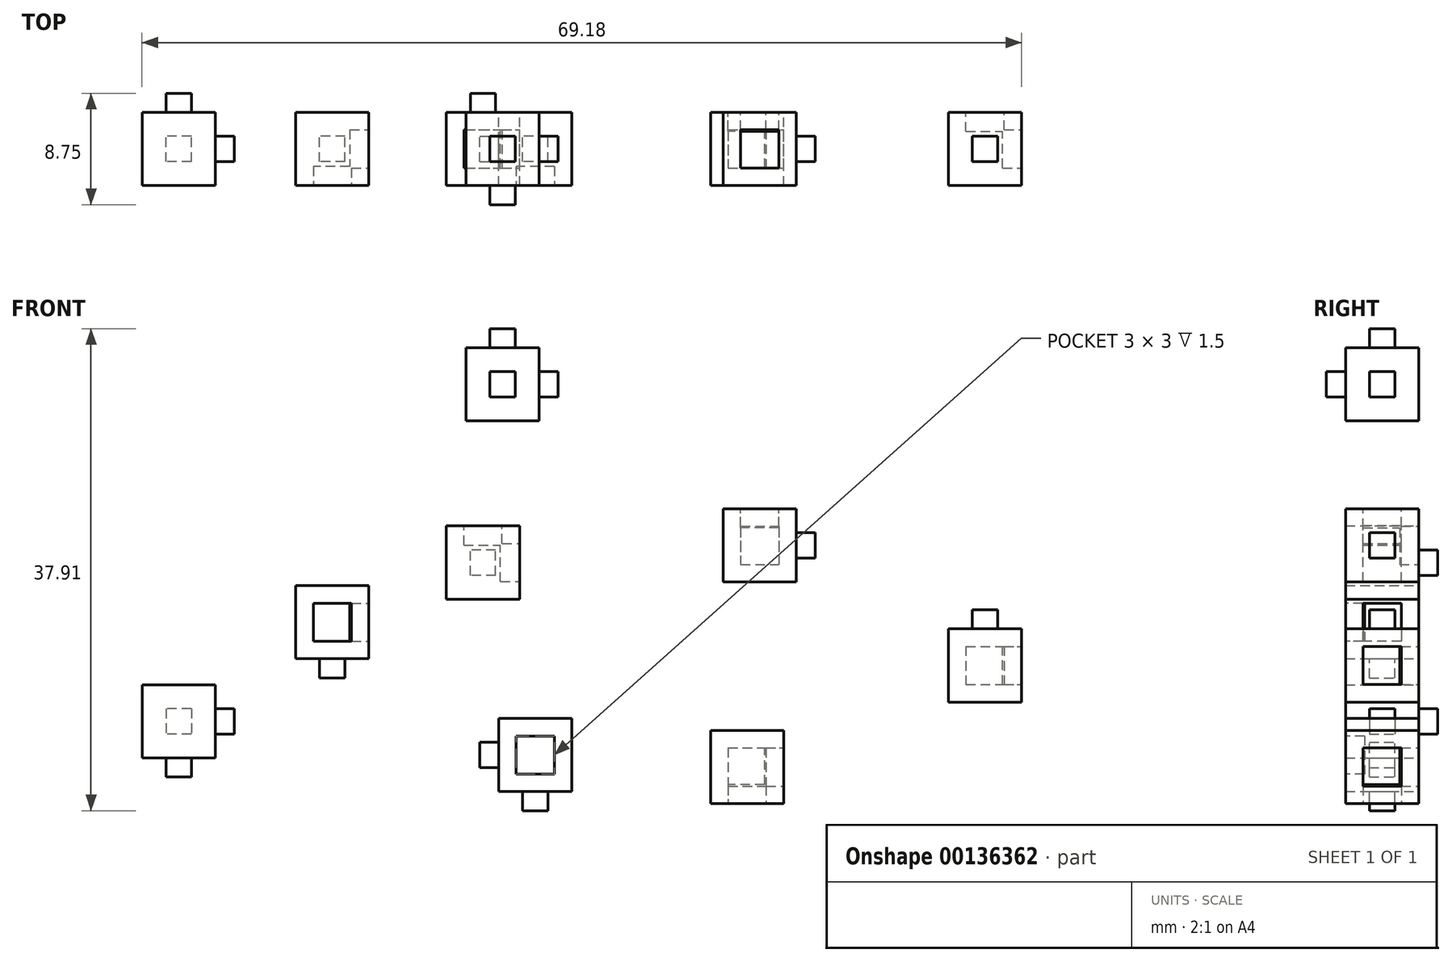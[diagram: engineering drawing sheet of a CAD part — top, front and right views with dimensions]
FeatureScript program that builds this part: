
annotation { "Feature Type Name" : "Feature", "Feature Type Description" : "" }
export const myFeature = defineFeature(function(context is Context, id is Id, definition is map)
    precondition{}
    {
        {
            var Q0;
            Q0=qCreatedBy(makeId("Front.planeOp"),FACE);
            var sketch = newSketch(context, id + "F0", { "sketchPlane" : qUnion([Q0])});
            skLineSegment(sketch, "E0.bottom", {"start": v(-17.05, 10.62) * mm, "end": v(-11.3, 10.62) * mm});
            skLineSegment(sketch, "E0.top", {"start": v(-17.05, 4.87) * mm, "end": v(-11.3, 4.87) * mm});
            skLineSegment(sketch, "E0.left", {"start": v(-17.05, 10.62) * mm, "end": v(-17.05, 4.87) * mm});
            skLineSegment(sketch, "E0.right", {"start": v(-11.3, 10.62) * mm, "end": v(-11.3, 4.87) * mm});
            skLineSegment(sketch, "E1.bottom", {"start": v(4.72, 11.97) * mm, "end": v(10.47, 11.97) * mm});
            skLineSegment(sketch, "E1.top", {"start": v(4.72, 6.22) * mm, "end": v(10.47, 6.22) * mm});
            skLineSegment(sketch, "E1.left", {"start": v(4.72, 11.97) * mm, "end": v(4.72, 6.22) * mm});
            skLineSegment(sketch, "E1.right", {"start": v(10.47, 11.97) * mm, "end": v(10.47, 6.22) * mm});
            skLineSegment(sketch, "E2.bottom", {"start": v(3.72, -5.46) * mm, "end": v(9.47, -5.46) * mm});
            skLineSegment(sketch, "E2.top", {"start": v(3.72, -11.2) * mm, "end": v(9.47, -11.2) * mm});
            skLineSegment(sketch, "E2.left", {"start": v(3.72, -5.46) * mm, "end": v(3.72, -11.2) * mm});
            skLineSegment(sketch, "E2.right", {"start": v(9.47, -5.46) * mm, "end": v(9.47, -11.2) * mm});
            skLineSegment(sketch, "E3.bottom", {"start": v(-12.94, -4.52) * mm, "end": v(-7.19, -4.52) * mm});
            skLineSegment(sketch, "E3.top", {"start": v(-12.94, -10.27) * mm, "end": v(-7.19, -10.27) * mm});
            skLineSegment(sketch, "E3.left", {"start": v(-12.94, -4.52) * mm, "end": v(-12.94, -10.27) * mm});
            skLineSegment(sketch, "E3.right", {"start": v(-7.19, -4.52) * mm, "end": v(-7.19, -10.27) * mm});
            skLineSegment(sketch, "E4.bottom", {"start": v(22.44, 2.52) * mm, "end": v(28.2, 2.52) * mm});
            skLineSegment(sketch, "E4.top", {"start": v(22.44, -3.23) * mm, "end": v(28.2, -3.23) * mm});
            skLineSegment(sketch, "E4.left", {"start": v(22.44, 2.52) * mm, "end": v(22.44, -3.23) * mm});
            skLineSegment(sketch, "E4.right", {"start": v(28.2, 2.52) * mm, "end": v(28.2, -3.23) * mm});
            skLineSegment(sketch, "E5.bottom", {"start": v(-28.9, 5.92) * mm, "end": v(-23.15, 5.92) * mm});
            skLineSegment(sketch, "E5.top", {"start": v(-28.9, 0.17) * mm, "end": v(-23.15, 0.17) * mm});
            skLineSegment(sketch, "E5.left", {"start": v(-28.9, 5.92) * mm, "end": v(-28.9, 0.17) * mm});
            skLineSegment(sketch, "E5.right", {"start": v(-23.15, 5.92) * mm, "end": v(-23.15, 0.17) * mm});
            skLineSegment(sketch, "E6.bottom", {"start": v(-35.24, -1.88) * mm, "end": v(-40.99, -1.88) * mm});
            skLineSegment(sketch, "E6.top", {"start": v(-35.24, -7.63) * mm, "end": v(-40.99, -7.63) * mm});
            skLineSegment(sketch, "E6.left", {"start": v(-35.24, -1.88) * mm, "end": v(-35.24, -7.63) * mm});
            skLineSegment(sketch, "E6.right", {"start": v(-40.99, -1.88) * mm, "end": v(-40.99, -7.63) * mm});
            skLineSegment(sketch, "E7.bottom", {"start": v(-15.52, 24.64) * mm, "end": v(-9.77, 24.64) * mm});
            skLineSegment(sketch, "E7.top", {"start": v(-15.52, 18.9) * mm, "end": v(-9.77, 18.9) * mm});
            skLineSegment(sketch, "E7.left", {"start": v(-15.52, 24.64) * mm, "end": v(-15.52, 18.9) * mm});
            skLineSegment(sketch, "E7.right", {"start": v(-9.77, 24.64) * mm, "end": v(-9.77, 18.9) * mm});
            skSolve(sketch);
        }
        {
            var Q0;
            Q0=makeQuery(id+"F0.imprint","IMPRINT",FACE,{"disambiguationData":[TD([[makeQuery(id+"F0.imprint","IMPRINT",EDGE,{"derivedFrom":sQuery(id+"F0.wireOp",EDGE,"E7.bottom")}),-1.0]])]});
            var Q1;
            Q1=makeQuery(id+"F0.imprint","IMPRINT",FACE,{"disambiguationData":[TD([[makeQuery(id+"F0.imprint","IMPRINT",EDGE,{"derivedFrom":sQuery(id+"F0.wireOp",EDGE,"E0.bottom")}),-1.0]])]});
            var Q2;
            Q2=makeQuery(id+"F0.imprint","IMPRINT",FACE,{"disambiguationData":[TD([[makeQuery(id+"F0.imprint","IMPRINT",EDGE,{"derivedFrom":sQuery(id+"F0.wireOp",EDGE,"E5.bottom")}),-1.0]])]});
            var Q3;
            Q3=makeQuery(id+"F0.imprint","IMPRINT",FACE,{"disambiguationData":[TD([[makeQuery(id+"F0.imprint","IMPRINT",EDGE,{"derivedFrom":sQuery(id+"F0.wireOp",EDGE,"E6.bottom")}),1.0]])]});
            var Q4;
            Q4=makeQuery(id+"F0.imprint","IMPRINT",FACE,{"disambiguationData":[TD([[makeQuery(id+"F0.imprint","IMPRINT",EDGE,{"derivedFrom":sQuery(id+"F0.wireOp",EDGE,"E3.bottom")}),-1.0]])]});
            var Q5;
            Q5=makeQuery(id+"F0.imprint","IMPRINT",FACE,{"disambiguationData":[TD([[makeQuery(id+"F0.imprint","IMPRINT",EDGE,{"derivedFrom":sQuery(id+"F0.wireOp",EDGE,"E2.bottom")}),-1.0]])]});
            var Q6;
            Q6=makeQuery(id+"F0.imprint","IMPRINT",FACE,{"disambiguationData":[TD([[makeQuery(id+"F0.imprint","IMPRINT",EDGE,{"derivedFrom":sQuery(id+"F0.wireOp",EDGE,"E1.bottom")}),-1.0]])]});
            var Q7;
            Q7=makeQuery(id+"F0.imprint","IMPRINT",FACE,{"disambiguationData":[TD([[makeQuery(id+"F0.imprint","IMPRINT",EDGE,{"derivedFrom":sQuery(id+"F0.wireOp",EDGE,"E4.bottom")}),-1.0]])]});
            extrude(context, id + "F1", {"entities" : qUnion([Q0, Q1, Q2, Q3, Q4, Q5, Q6, Q7]), "depth" : 5.75 * mm});
        }
        {
            var Q0;
            Q0=makeQuery(id+"F1.opExtrude","CAP_FACE",FACE,{"disambiguationData":[OSD([sQuery(id+"F0.wireOp",EDGE,"E5.bottom"),sQuery(id+"F0.wireOp",EDGE,"E5.top"),sQuery(id+"F0.wireOp",EDGE,"E5.left"),sQuery(id+"F0.wireOp",EDGE,"E5.right")])],"isStart":false});
            var sketch = newSketch(context, id + "F2", { "sketchPlane" : qUnion([Q0])});
            skLineSegment(sketch, "E8.bottom", {"start": v(-24.52, 4.55) * mm, "end": v(-27.52, 4.55) * mm});
            skLineSegment(sketch, "E8.top", {"start": v(-24.52, 1.55) * mm, "end": v(-27.52, 1.55) * mm});
            skLineSegment(sketch, "E8.left", {"start": v(-24.52, 4.55) * mm, "end": v(-24.52, 1.55) * mm});
            skLineSegment(sketch, "E8.right", {"start": v(-27.52, 4.55) * mm, "end": v(-27.52, 1.55) * mm});
            skPoint(sketch, "E8.middle", {"position": v(-26.02, 3.05) * mm});
            skPoint(sketch, "E8.middle.positionSnap0", {"position": v(-28.9, 3.05) * mm});
            skPoint(sketch, "E8.middle.positionSnap1", {"position": v(-26.02, 5.92) * mm});
            skPoint(sketch, "E8.centerSnap0", {"position": v(-28.9, 3.05) * mm});
            skPoint(sketch, "E8.centerSnap1", {"position": v(-26.02, 5.92) * mm});
            skSolve(sketch);
        }
        {
            var Q0;
            Q0=makeQuery(id+"F1.opExtrude","SWEPT_FACE",FACE,{"disambiguationData":[OSD([sQuery(id+"F0.wireOp",EDGE,"E5.top")])]});
            var sketch = newSketch(context, id + "F3", { "sketchPlane" : qUnion([Q0])});
            skLineSegment(sketch, "E9.bottom", {"start": v(-25.02, 3.88) * mm, "end": v(-27.02, 3.88) * mm});
            skLineSegment(sketch, "E9.top", {"start": v(-25.02, 1.87) * mm, "end": v(-27.02, 1.87) * mm});
            skLineSegment(sketch, "E9.left", {"start": v(-25.02, 3.88) * mm, "end": v(-25.02, 1.88) * mm});
            skLineSegment(sketch, "E9.right", {"start": v(-27.02, 3.88) * mm, "end": v(-27.02, 1.88) * mm});
            skPoint(sketch, "E9.middle", {"position": v(-26.02, 2.88) * mm});
            skPoint(sketch, "E9.middle.positionSnap0", {"position": v(-28.9, 2.88) * mm});
            skPoint(sketch, "E9.middle.positionSnap1", {"position": v(-26.02, 5.75) * mm});
            skPoint(sketch, "E9.centerSnap0", {"position": v(-28.9, 2.88) * mm});
            skPoint(sketch, "E9.centerSnap1", {"position": v(-26.02, 5.75) * mm});
            skSolve(sketch);
        }
        {
            var Q0;
            Q0=makeQuery(id+"F2.imprint","IMPRINT",FACE,{"disambiguationData":[TD([[makeQuery(id+"F2.imprint","IMPRINT",EDGE,{"derivedFrom":sQuery(id+"F2.wireOp",EDGE,"E8.bottom")}),1.0]])]});
            extrude(context, id + "F4", {"entities" : qUnion([Q0]), "operationType" : NewBodyOperationType.REMOVE, "oppositeDirection" : true, "depth" : 1.5 * mm});
        }
        {
            var Q0;
            Q0=makeQuery(id+"F3.imprint","IMPRINT",FACE,{"disambiguationData":[TD([[makeQuery(id+"F3.imprint","IMPRINT",EDGE,{"derivedFrom":sQuery(id+"F3.wireOp",EDGE,"E9.bottom")}),1.0]])]});
            extrude(context, id + "F5", {"entities" : qUnion([Q0]), "operationType" : NewBodyOperationType.ADD, "depth" : 1.5 * mm});
        }
        {
            var Q0;
            Q0=makeQuery(id+"F1.opExtrude","SWEPT_FACE",FACE,{"disambiguationData":[OSD([sQuery(id+"F0.wireOp",EDGE,"E5.right")])]});
            var sketch = newSketch(context, id + "F6", { "sketchPlane" : qUnion([Q0])});
            skLineSegment(sketch, "E10.bottom", {"start": v(-1.38, 4.55) * mm, "end": v(-4.38, 4.55) * mm});
            skLineSegment(sketch, "E10.top", {"start": v(-1.38, 1.55) * mm, "end": v(-4.38, 1.55) * mm});
            skLineSegment(sketch, "E10.left", {"start": v(-1.38, 4.55) * mm, "end": v(-1.38, 1.55) * mm});
            skLineSegment(sketch, "E10.right", {"start": v(-4.38, 4.55) * mm, "end": v(-4.38, 1.55) * mm});
            skPoint(sketch, "E10.middle", {"position": v(-2.88, 3.05) * mm});
            skPoint(sketch, "E10.middle.positionSnap0", {"position": v(-2.88, 0.17) * mm});
            skPoint(sketch, "E10.middle.positionSnap1", {"position": v(-5.75, 3.05) * mm});
            skPoint(sketch, "E10.centerSnap0", {"position": v(-2.88, 0.17) * mm});
            skPoint(sketch, "E10.centerSnap1", {"position": v(-5.75, 3.05) * mm});
            skSolve(sketch);
        }
        {
            var Q0;
            Q0 = qSketchRegion(id + "F6", true);
            extrude(context, id + "F7", {"entities" : qUnion([Q0]), "operationType" : NewBodyOperationType.REMOVE, "oppositeDirection" : true, "depth" : 1.5 * mm});
        }
        {
            var Q0;
            Q0=makeQuery(id+"F1.opExtrude","CAP_FACE",FACE,{"disambiguationData":[OSD([sQuery(id+"F0.wireOp",EDGE,"E6.bottom"),sQuery(id+"F0.wireOp",EDGE,"E6.top"),sQuery(id+"F0.wireOp",EDGE,"E6.left"),sQuery(id+"F0.wireOp",EDGE,"E6.right")])],"isStart":true});
            var sketch = newSketch(context, id + "F8", { "sketchPlane" : qUnion([Q0])});
            skLineSegment(sketch, "E11.bottom", {"start": v(37.11, -3.75) * mm, "end": v(39.11, -3.75) * mm});
            skLineSegment(sketch, "E11.top", {"start": v(37.11, -5.75) * mm, "end": v(39.11, -5.75) * mm});
            skLineSegment(sketch, "E11.left", {"start": v(37.11, -3.75) * mm, "end": v(37.11, -5.75) * mm});
            skLineSegment(sketch, "E11.right", {"start": v(39.11, -3.75) * mm, "end": v(39.11, -5.75) * mm});
            skPoint(sketch, "E11.middle", {"position": v(38.11, -4.75) * mm});
            skPoint(sketch, "E11.middle.positionSnap0", {"position": v(40.99, -4.75) * mm});
            skPoint(sketch, "E11.middle.positionSnap1", {"position": v(38.11, -7.63) * mm});
            skPoint(sketch, "E11.centerSnap0", {"position": v(40.99, -4.75) * mm});
            skPoint(sketch, "E11.centerSnap1", {"position": v(38.11, -7.63) * mm});
            skSolve(sketch);
        }
        {
            var Q0;
            Q0=makeQuery(id+"F8.imprint","IMPRINT",FACE,{"disambiguationData":[TD([[makeQuery(id+"F8.imprint","IMPRINT",EDGE,{"derivedFrom":sQuery(id+"F8.wireOp",EDGE,"E11.bottom")}),-1.0]])]});
            extrude(context, id + "F9", {"entities" : qUnion([Q0]), "operationType" : NewBodyOperationType.ADD, "depth" : 1.5 * mm});
        }
        {
            var Q0;
            Q0=makeQuery(id+"F1.opExtrude","SWEPT_FACE",FACE,{"disambiguationData":[OSD([sQuery(id+"F0.wireOp",EDGE,"E6.left")])]});
            var sketch = newSketch(context, id + "F10", { "sketchPlane" : qUnion([Q0])});
            skLineSegment(sketch, "E12.bottom", {"start": v(-3.88, -3.75) * mm, "end": v(-1.88, -3.75) * mm});
            skLineSegment(sketch, "E12.top", {"start": v(-3.87, -5.75) * mm, "end": v(-1.88, -5.75) * mm});
            skLineSegment(sketch, "E12.left", {"start": v(-3.88, -3.75) * mm, "end": v(-3.87, -5.75) * mm});
            skLineSegment(sketch, "E12.right", {"start": v(-1.88, -3.75) * mm, "end": v(-1.88, -5.75) * mm});
            skPoint(sketch, "E12.middle", {"position": v(-2.88, -4.75) * mm});
            skPoint(sketch, "E12.middle.positionSnap0", {"position": v(-5.75, -4.75) * mm});
            skPoint(sketch, "E12.middle.positionSnap1", {"position": v(-2.88, -7.63) * mm});
            skPoint(sketch, "E12.centerSnap0", {"position": v(-5.75, -4.75) * mm});
            skPoint(sketch, "E12.centerSnap1", {"position": v(-2.88, -7.63) * mm});
            skSolve(sketch);
        }
        {
            var Q0;
            Q0=makeQuery(id+"F10.imprint","IMPRINT",FACE,{"disambiguationData":[TD([[makeQuery(id+"F10.imprint","IMPRINT",EDGE,{"derivedFrom":sQuery(id+"F10.wireOp",EDGE,"E12.bottom")}),-1.0]])]});
            extrude(context, id + "F11", {"entities" : qUnion([Q0]), "operationType" : NewBodyOperationType.ADD, "depth" : 1.5 * mm});
        }
        {
            var Q0;
            Q0=makeQuery(id+"F1.opExtrude","SWEPT_FACE",FACE,{"disambiguationData":[OSD([sQuery(id+"F0.wireOp",EDGE,"E6.top")])]});
            var sketch = newSketch(context, id + "F12", { "sketchPlane" : qUnion([Q0])});
            skLineSegment(sketch, "E13.bottom", {"start": v(-37.11, 3.87) * mm, "end": v(-39.11, 3.87) * mm});
            skLineSegment(sketch, "E13.top", {"start": v(-37.11, 1.87) * mm, "end": v(-39.11, 1.87) * mm});
            skLineSegment(sketch, "E13.left", {"start": v(-37.11, 3.87) * mm, "end": v(-37.11, 1.87) * mm});
            skLineSegment(sketch, "E13.right", {"start": v(-39.11, 3.87) * mm, "end": v(-39.11, 1.87) * mm});
            skPoint(sketch, "E13.middle", {"position": v(-38.11, 2.88) * mm});
            skPoint(sketch, "E13.middle.positionSnap0", {"position": v(-40.99, 2.88) * mm});
            skPoint(sketch, "E13.middle.positionSnap1", {"position": v(-38.11, 5.75) * mm});
            skPoint(sketch, "E13.centerSnap0", {"position": v(-40.99, 2.88) * mm});
            skPoint(sketch, "E13.centerSnap1", {"position": v(-38.11, 5.75) * mm});
            skSolve(sketch);
        }
        {
            var Q0;
            Q0 = qSketchRegion(id + "F12", true);
            extrude(context, id + "F13", {"entities" : qUnion([Q0]), "operationType" : NewBodyOperationType.ADD, "depth" : 1.5 * mm});
        }
        {
            var Q0;
            Q0=makeQuery(id+"F1.opExtrude","CAP_FACE",FACE,{"disambiguationData":[OSD([sQuery(id+"F0.wireOp",EDGE,"E3.bottom"),sQuery(id+"F0.wireOp",EDGE,"E3.top"),sQuery(id+"F0.wireOp",EDGE,"E3.left"),sQuery(id+"F0.wireOp",EDGE,"E3.right")])],"isStart":false});
            var sketch = newSketch(context, id + "F14", { "sketchPlane" : qUnion([Q0])});
            skLineSegment(sketch, "E14.bottom", {"start": v(-8.56, -5.9) * mm, "end": v(-11.56, -5.9) * mm});
            skLineSegment(sketch, "E14.top", {"start": v(-8.56, -8.9) * mm, "end": v(-11.56, -8.9) * mm});
            skLineSegment(sketch, "E14.left", {"start": v(-8.56, -5.9) * mm, "end": v(-8.56, -8.9) * mm});
            skLineSegment(sketch, "E14.right", {"start": v(-11.56, -5.9) * mm, "end": v(-11.56, -8.9) * mm});
            skPoint(sketch, "E14.middle", {"position": v(-10.06, -7.4) * mm});
            skPoint(sketch, "E14.middle.positionSnap0", {"position": v(-12.94, -7.4) * mm});
            skPoint(sketch, "E14.middle.positionSnap1", {"position": v(-10.06, -4.52) * mm});
            skPoint(sketch, "E14.centerSnap0", {"position": v(-12.94, -7.4) * mm});
            skPoint(sketch, "E14.centerSnap1", {"position": v(-10.06, -4.52) * mm});
            skSolve(sketch);
        }
        {
            var Q0;
            Q0 = qSketchRegion(id + "F14", true);
            extrude(context, id + "F15", {"entities" : qUnion([Q0]), "operationType" : NewBodyOperationType.REMOVE, "oppositeDirection" : true, "depth" : 1.5 * mm});
        }
        {
            var Q0;
            Q0=makeQuery(id+"F1.opExtrude","SWEPT_FACE",FACE,{"disambiguationData":[OSD([sQuery(id+"F0.wireOp",EDGE,"E3.top")])]});
            var sketch = newSketch(context, id + "F16", { "sketchPlane" : qUnion([Q0])});
            skLineSegment(sketch, "E15.bottom", {"start": v(-9.06, 3.87) * mm, "end": v(-11.06, 3.87) * mm});
            skLineSegment(sketch, "E15.top", {"start": v(-9.06, 1.87) * mm, "end": v(-11.06, 1.88) * mm});
            skLineSegment(sketch, "E15.left", {"start": v(-9.06, 3.87) * mm, "end": v(-9.06, 1.87) * mm});
            skLineSegment(sketch, "E15.right", {"start": v(-11.06, 3.87) * mm, "end": v(-11.06, 1.88) * mm});
            skPoint(sketch, "E15.middle", {"position": v(-10.06, 2.88) * mm});
            skPoint(sketch, "E15.middle.positionSnap0", {"position": v(-12.94, 2.88) * mm});
            skPoint(sketch, "E15.middle.positionSnap1", {"position": v(-10.06, 5.75) * mm});
            skPoint(sketch, "E15.centerSnap0", {"position": v(-12.94, 2.88) * mm});
            skPoint(sketch, "E15.centerSnap1", {"position": v(-10.06, 5.75) * mm});
            skSolve(sketch);
        }
        {
            var Q0;
            Q0=makeQuery(id+"F16.imprint","IMPRINT",FACE,{"disambiguationData":[TD([[makeQuery(id+"F16.imprint","IMPRINT",EDGE,{"derivedFrom":sQuery(id+"F16.wireOp",EDGE,"E15.bottom")}),1.0]])]});
            extrude(context, id + "F17", {"entities" : qUnion([Q0]), "operationType" : NewBodyOperationType.ADD, "depth" : 1.5 * mm});
        }
        {
            var Q0;
            Q0=makeQuery(id+"F1.opExtrude","SWEPT_FACE",FACE,{"disambiguationData":[OSD([sQuery(id+"F0.wireOp",EDGE,"E3.left")])]});
            var sketch = newSketch(context, id + "F18", { "sketchPlane" : qUnion([Q0])});
            skLineSegment(sketch, "E16.bottom", {"start": v(3.88, -8.4) * mm, "end": v(1.88, -8.4) * mm});
            skLineSegment(sketch, "E16.top", {"start": v(3.88, -6.4) * mm, "end": v(1.88, -6.4) * mm});
            skLineSegment(sketch, "E16.left", {"start": v(3.88, -8.4) * mm, "end": v(3.88, -6.4) * mm});
            skLineSegment(sketch, "E16.right", {"start": v(1.88, -8.4) * mm, "end": v(1.88, -6.4) * mm});
            skPoint(sketch, "E16.middle", {"position": v(2.88, -7.4) * mm});
            skPoint(sketch, "E16.middle.positionSnap0", {"position": v(2.88, -4.52) * mm});
            skPoint(sketch, "E16.middle.positionSnap1", {"position": v(5.75, -7.4) * mm});
            skPoint(sketch, "E16.centerSnap0", {"position": v(2.88, -4.52) * mm});
            skPoint(sketch, "E16.centerSnap1", {"position": v(5.75, -7.4) * mm});
            skSolve(sketch);
        }
        {
            var Q0;
            Q0 = qSketchRegion(id + "F18", true);
            extrude(context, id + "F19", {"entities" : qUnion([Q0]), "operationType" : NewBodyOperationType.ADD, "depth" : 1.5 * mm});
        }
        {
            var Q0;
            Q0=makeQuery(id+"F1.opExtrude","SWEPT_FACE",FACE,{"disambiguationData":[OSD([sQuery(id+"F0.wireOp",EDGE,"E4.right")])]});
            var sketch = newSketch(context, id + "F20", { "sketchPlane" : qUnion([Q0])});
            skLineSegment(sketch, "E17.bottom", {"start": v(-4.38, 1.15) * mm, "end": v(-1.37, 1.15) * mm});
            skLineSegment(sketch, "E17.top", {"start": v(-4.38, -1.85) * mm, "end": v(-1.38, -1.85) * mm});
            skLineSegment(sketch, "E17.left", {"start": v(-4.38, 1.15) * mm, "end": v(-4.38, -1.85) * mm});
            skLineSegment(sketch, "E17.right", {"start": v(-1.37, 1.15) * mm, "end": v(-1.38, -1.85) * mm});
            skPoint(sketch, "E17.middle", {"position": v(-2.88, -0.35) * mm});
            skPoint(sketch, "E17.middle.positionSnap0", {"position": v(-2.88, -3.23) * mm});
            skPoint(sketch, "E17.middle.positionSnap1", {"position": v(-5.75, -0.35) * mm});
            skPoint(sketch, "E17.centerSnap0", {"position": v(-2.88, -3.23) * mm});
            skPoint(sketch, "E17.centerSnap1", {"position": v(-5.75, -0.35) * mm});
            skSolve(sketch);
        }
        {
            var Q0;
            Q0 = qSketchRegion(id + "F20", true);
            extrude(context, id + "F21", {"entities" : qUnion([Q0]), "operationType" : NewBodyOperationType.REMOVE, "oppositeDirection" : true, "depth" : 1.5 * mm});
        }
        {
            var Q0;
            Q0=makeQuery(id+"F1.opExtrude","CAP_FACE",FACE,{"disambiguationData":[OSD([sQuery(id+"F0.wireOp",EDGE,"E4.bottom"),sQuery(id+"F0.wireOp",EDGE,"E4.top"),sQuery(id+"F0.wireOp",EDGE,"E4.left"),sQuery(id+"F0.wireOp",EDGE,"E4.right")])],"isStart":true});
            var sketch = newSketch(context, id + "F22", { "sketchPlane" : qUnion([Q0])});
            skPoint(sketch, "E18.middle", {"position": v(-25.32, 0) * mm});
            skPoint(sketch, "E18.middle.positionSnap0", {"position": v(-25.32, -3.23) * mm});
            skPoint(sketch, "E18.centerSnap0", {"position": v(-25.32, -3.23) * mm});
            skLineSegment(sketch, "E19.bottom", {"start": v(-23.82, 1.15) * mm, "end": v(-26.82, 1.15) * mm});
            skLineSegment(sketch, "E19.top", {"start": v(-23.82, -1.85) * mm, "end": v(-26.82, -1.85) * mm});
            skLineSegment(sketch, "E19.left", {"start": v(-23.82, 1.15) * mm, "end": v(-23.82, -1.85) * mm});
            skLineSegment(sketch, "E19.right", {"start": v(-26.82, 1.15) * mm, "end": v(-26.82, -1.85) * mm});
            skPoint(sketch, "E19.middle", {"position": v(-25.32, -0.35) * mm});
            skPoint(sketch, "E19.middle.positionSnap0", {"position": v(-28.2, -0.35) * mm});
            skPoint(sketch, "E19.centerSnap0", {"position": v(-28.2, -0.35) * mm});
            skSolve(sketch);
        }
        {
            var Q0;
            Q0 = qSketchRegion(id + "F22", true);
            extrude(context, id + "F23", {"entities" : qUnion([Q0]), "operationType" : NewBodyOperationType.REMOVE, "oppositeDirection" : true, "depth" : 1.5 * mm});
        }
        {
            var Q0;
            Q0 = qSketchRegion(id + "F22", true);
            extrude(context, id + "F24", {"entities" : qUnion([Q0]), "operationType" : NewBodyOperationType.REMOVE, "oppositeDirection" : true, "depth" : 1.5 * mm});
        }
        {
            var Q0;
            Q0=makeQuery(id+"F1.opExtrude","SWEPT_FACE",FACE,{"disambiguationData":[OSD([sQuery(id+"F0.wireOp",EDGE,"E4.bottom")])]});
            var sketch = newSketch(context, id + "F25", { "sketchPlane" : qUnion([Q0])});
            skLineSegment(sketch, "E20.bottom", {"start": v(24.32, -3.88) * mm, "end": v(26.32, -3.88) * mm});
            skLineSegment(sketch, "E20.top", {"start": v(24.32, -1.88) * mm, "end": v(26.32, -1.88) * mm});
            skLineSegment(sketch, "E20.left", {"start": v(24.32, -3.88) * mm, "end": v(24.32, -1.88) * mm});
            skLineSegment(sketch, "E20.right", {"start": v(26.32, -3.88) * mm, "end": v(26.32, -1.88) * mm});
            skPoint(sketch, "E20.middle", {"position": v(25.32, -2.88) * mm});
            skPoint(sketch, "E20.middle.positionSnap0", {"position": v(25.32, -5.75) * mm});
            skPoint(sketch, "E20.middle.positionSnap1", {"position": v(28.2, -2.88) * mm});
            skPoint(sketch, "E20.centerSnap0", {"position": v(25.32, -5.75) * mm});
            skPoint(sketch, "E20.centerSnap1", {"position": v(28.2, -2.88) * mm});
            skSolve(sketch);
        }
        {
            var Q0;
            Q0 = qSketchRegion(id + "F25", true);
            var Q1;
            Q1 = qSketchRegion(id + "F28", true);
            extrude(context, id + "F26", {"entities" : qUnion([Q0, Q1]), "operationType" : NewBodyOperationType.ADD, "depth" : 1.5 * mm});
        }
        {
            var Q0;
            Q0=makeQuery(id+"F1.opExtrude","CAP_FACE",FACE,{"disambiguationData":[OSD([sQuery(id+"F0.wireOp",EDGE,"E7.bottom"),sQuery(id+"F0.wireOp",EDGE,"E7.top"),sQuery(id+"F0.wireOp",EDGE,"E7.left"),sQuery(id+"F0.wireOp",EDGE,"E7.right")])],"isStart":false});
            var sketch = newSketch(context, id + "F27", { "sketchPlane" : qUnion([Q0])});
            skLineSegment(sketch, "E21.bottom", {"start": v(-11.65, 20.77) * mm, "end": v(-13.65, 20.77) * mm});
            skLineSegment(sketch, "E21.top", {"start": v(-11.65, 22.77) * mm, "end": v(-13.65, 22.77) * mm});
            skLineSegment(sketch, "E21.left", {"start": v(-11.65, 20.77) * mm, "end": v(-11.65, 22.77) * mm});
            skLineSegment(sketch, "E21.right", {"start": v(-13.65, 20.77) * mm, "end": v(-13.65, 22.77) * mm});
            skPoint(sketch, "E21.middle", {"position": v(-12.65, 21.77) * mm});
            skPoint(sketch, "E21.middle.positionSnap0", {"position": v(-12.65, 24.64) * mm});
            skPoint(sketch, "E21.middle.positionSnap1", {"position": v(-9.77, 21.77) * mm});
            skPoint(sketch, "E21.centerSnap0", {"position": v(-12.65, 24.64) * mm});
            skPoint(sketch, "E21.centerSnap1", {"position": v(-9.77, 21.77) * mm});
            skSolve(sketch);
        }
        {
            var Q0;
            Q0=makeQuery(id+"F1.opExtrude","SWEPT_FACE",FACE,{"disambiguationData":[OSD([sQuery(id+"F0.wireOp",EDGE,"E7.bottom")])]});
            var sketch = newSketch(context, id + "F28", { "sketchPlane" : qUnion([Q0])});
            skLineSegment(sketch, "E22.bottom", {"start": v(-11.65, -3.88) * mm, "end": v(-13.65, -3.88) * mm});
            skLineSegment(sketch, "E22.top", {"start": v(-11.65, -1.88) * mm, "end": v(-13.65, -1.88) * mm});
            skLineSegment(sketch, "E22.left", {"start": v(-11.65, -3.88) * mm, "end": v(-11.65, -1.88) * mm});
            skLineSegment(sketch, "E22.right", {"start": v(-13.65, -3.88) * mm, "end": v(-13.65, -1.88) * mm});
            skPoint(sketch, "E22.middle", {"position": v(-12.65, -2.88) * mm});
            skPoint(sketch, "E22.middle.positionSnap0", {"position": v(-12.65, 0) * mm});
            skPoint(sketch, "E22.middle.positionSnap1", {"position": v(-9.77, -2.88) * mm});
            skPoint(sketch, "E22.centerSnap0", {"position": v(-12.65, 0) * mm});
            skPoint(sketch, "E22.centerSnap1", {"position": v(-9.77, -2.88) * mm});
            skSolve(sketch);
        }
        {
            var Q0;
            Q0=makeQuery(id+"F28.imprint","IMPRINT",FACE,{"disambiguationData":[TD([[makeQuery(id+"F28.imprint","IMPRINT",EDGE,{"derivedFrom":sQuery(id+"F28.wireOp",EDGE,"E22.bottom")}),-1.0]])]});
            extrude(context, id + "F29", {"entities" : qUnion([Q0]), "operationType" : NewBodyOperationType.ADD, "depth" : 1.5 * mm});
        }
        {
            var Q0;
            Q0 = qSketchRegion(id + "F27", true);
            extrude(context, id + "F30", {"entities" : qUnion([Q0]), "operationType" : NewBodyOperationType.ADD, "depth" : 1.5 * mm});
        }
        {
            var Q0;
            Q0=makeQuery(id+"F1.opExtrude","SWEPT_FACE",FACE,{"disambiguationData":[OSD([sQuery(id+"F0.wireOp",EDGE,"E7.right")])]});
            var sketch = newSketch(context, id + "F31", { "sketchPlane" : qUnion([Q0])});
            skLineSegment(sketch, "E23.bottom", {"start": v(-1.88, 20.77) * mm, "end": v(-3.88, 20.77) * mm});
            skLineSegment(sketch, "E23.top", {"start": v(-1.88, 22.77) * mm, "end": v(-3.88, 22.77) * mm});
            skLineSegment(sketch, "E23.left", {"start": v(-1.88, 20.77) * mm, "end": v(-1.88, 22.77) * mm});
            skLineSegment(sketch, "E23.right", {"start": v(-3.88, 20.77) * mm, "end": v(-3.88, 22.77) * mm});
            skPoint(sketch, "E23.middle", {"position": v(-2.88, 21.77) * mm});
            skPoint(sketch, "E23.middle.positionSnap0", {"position": v(0, 21.77) * mm});
            skPoint(sketch, "E23.middle.positionSnap1", {"position": v(-2.88, 18.9) * mm});
            skPoint(sketch, "E23.centerSnap0", {"position": v(0, 21.77) * mm});
            skPoint(sketch, "E23.centerSnap1", {"position": v(-2.88, 18.9) * mm});
            skSolve(sketch);
        }
        {
            var Q0;
            Q0 = qSketchRegion(id + "F31", true);
            extrude(context, id + "F32", {"entities" : qUnion([Q0]), "operationType" : NewBodyOperationType.ADD, "depth" : 1.5 * mm});
        }
        {
            var Q0;
            Q0=makeQuery(id+"F1.opExtrude","SWEPT_FACE",FACE,{"disambiguationData":[OSD([sQuery(id+"F0.wireOp",EDGE,"E1.bottom")])]});
            var sketch = newSketch(context, id + "F33", { "sketchPlane" : qUnion([Q0])});
            skLineSegment(sketch, "E24.bottom", {"start": v(9.1, -4.38) * mm, "end": v(6.1, -4.38) * mm});
            skLineSegment(sketch, "E24.top", {"start": v(9.1, -1.37) * mm, "end": v(6.1, -1.38) * mm});
            skLineSegment(sketch, "E24.left", {"start": v(9.1, -4.38) * mm, "end": v(9.1, -1.37) * mm});
            skLineSegment(sketch, "E24.right", {"start": v(6.1, -4.38) * mm, "end": v(6.1, -1.37) * mm});
            skPoint(sketch, "E24.middle", {"position": v(7.6, -2.88) * mm});
            skPoint(sketch, "E24.middle.positionSnap0", {"position": v(7.6, 0) * mm});
            skPoint(sketch, "E24.middle.positionSnap1", {"position": v(10.47, -2.88) * mm});
            skPoint(sketch, "E24.centerSnap0", {"position": v(7.6, 0) * mm});
            skPoint(sketch, "E24.centerSnap1", {"position": v(10.47, -2.88) * mm});
            skSolve(sketch);
        }
        {
            var Q0;
            Q0=makeQuery(id+"F33.imprint","IMPRINT",FACE,{"disambiguationData":[TD([[makeQuery(id+"F33.imprint","IMPRINT",EDGE,{"derivedFrom":sQuery(id+"F33.wireOp",EDGE,"E24.bottom")}),-1.0]])]});
            extrude(context, id + "F34", {"entities" : qUnion([Q0]), "operationType" : NewBodyOperationType.REMOVE, "oppositeDirection" : true, "depth" : 1.5 * mm});
        }
        {
            var Q0;
            Q0=makeQuery(id+"F1.opExtrude","CAP_FACE",FACE,{"disambiguationData":[OSD([sQuery(id+"F0.wireOp",EDGE,"E1.bottom"),sQuery(id+"F0.wireOp",EDGE,"E1.top"),sQuery(id+"F0.wireOp",EDGE,"E1.left"),sQuery(id+"F0.wireOp",EDGE,"E1.right")])],"isStart":true});
            var sketch = newSketch(context, id + "F35", { "sketchPlane" : qUnion([Q0])});
            skLineSegment(sketch, "E25.bottom", {"start": v(-6.1, 10.6) * mm, "end": v(-9.1, 10.6) * mm});
            skLineSegment(sketch, "E25.top", {"start": v(-6.1, 7.6) * mm, "end": v(-9.1, 7.6) * mm});
            skLineSegment(sketch, "E25.left", {"start": v(-6.1, 10.6) * mm, "end": v(-6.1, 7.6) * mm});
            skLineSegment(sketch, "E25.right", {"start": v(-9.1, 10.6) * mm, "end": v(-9.1, 7.6) * mm});
            skPoint(sketch, "E25.middle", {"position": v(-7.6, 9.1) * mm});
            skPoint(sketch, "E25.middle.positionSnap0", {"position": v(-7.6, 6.22) * mm});
            skPoint(sketch, "E25.middle.positionSnap1", {"position": v(-10.47, 9.1) * mm});
            skPoint(sketch, "E25.centerSnap0", {"position": v(-7.6, 6.22) * mm});
            skPoint(sketch, "E25.centerSnap1", {"position": v(-10.47, 9.1) * mm});
            skSolve(sketch);
        }
        {
            var Q0;
            Q0 = qSketchRegion(id + "F35", true);
            extrude(context, id + "F36", {"entities" : qUnion([Q0]), "operationType" : NewBodyOperationType.REMOVE, "oppositeDirection" : true, "depth" : 1.5 * mm});
        }
        {
            var Q0;
            Q0=makeQuery(id+"F1.opExtrude","SWEPT_FACE",FACE,{"disambiguationData":[OSD([sQuery(id+"F0.wireOp",EDGE,"E1.right")])]});
            var sketch = newSketch(context, id + "F37", { "sketchPlane" : qUnion([Q0])});
            skLineSegment(sketch, "E26.bottom", {"start": v(-1.88, 10.1) * mm, "end": v(-3.88, 10.1) * mm});
            skLineSegment(sketch, "E26.top", {"start": v(-1.88, 8.1) * mm, "end": v(-3.88, 8.1) * mm});
            skLineSegment(sketch, "E26.left", {"start": v(-1.88, 10.1) * mm, "end": v(-1.88, 8.1) * mm});
            skLineSegment(sketch, "E26.right", {"start": v(-3.88, 10.1) * mm, "end": v(-3.88, 8.1) * mm});
            skPoint(sketch, "E26.middle", {"position": v(-2.88, 9.1) * mm});
            skPoint(sketch, "E26.middle.positionSnap0", {"position": v(-2.88, 6.22) * mm});
            skPoint(sketch, "E26.middle.positionSnap1", {"position": v(0, 9.1) * mm});
            skPoint(sketch, "E26.centerSnap0", {"position": v(-2.88, 6.22) * mm});
            skPoint(sketch, "E26.centerSnap1", {"position": v(0, 9.1) * mm});
            skSolve(sketch);
        }
        {
            var Q0;
            Q0 = qSketchRegion(id + "F37", true);
            extrude(context, id + "F38", {"entities" : qUnion([Q0]), "operationType" : NewBodyOperationType.ADD, "depth" : 1.5 * mm});
        }
        {
            var Q0;
            Q0=makeQuery(id+"F1.opExtrude","CAP_FACE",FACE,{"disambiguationData":[OSD([sQuery(id+"F0.wireOp",EDGE,"E0.bottom"),sQuery(id+"F0.wireOp",EDGE,"E0.top"),sQuery(id+"F0.wireOp",EDGE,"E0.left"),sQuery(id+"F0.wireOp",EDGE,"E0.right")])],"isStart":true});
            var sketch = newSketch(context, id + "F39", { "sketchPlane" : qUnion([Q0])});
            skLineSegment(sketch, "E27.bottom", {"start": v(13.17, 6.74) * mm, "end": v(15.17, 6.74) * mm});
            skLineSegment(sketch, "E27.top", {"start": v(13.17, 8.74) * mm, "end": v(15.17, 8.74) * mm});
            skLineSegment(sketch, "E27.left", {"start": v(13.17, 6.74) * mm, "end": v(13.17, 8.74) * mm});
            skLineSegment(sketch, "E27.right", {"start": v(15.17, 6.74) * mm, "end": v(15.17, 8.74) * mm});
            skPoint(sketch, "E27.middle", {"position": v(14.17, 7.74) * mm});
            skPoint(sketch, "E27.middle.positionSnap0", {"position": v(17.05, 7.74) * mm});
            skPoint(sketch, "E27.middle.positionSnap1", {"position": v(14.17, 4.87) * mm});
            skPoint(sketch, "E27.centerSnap0", {"position": v(17.05, 7.74) * mm});
            skPoint(sketch, "E27.centerSnap1", {"position": v(14.17, 4.87) * mm});
            skSolve(sketch);
        }
        {
            var Q0;
            Q0=makeQuery(id+"F39.imprint","IMPRINT",FACE,{"disambiguationData":[TD([[makeQuery(id+"F39.imprint","IMPRINT",EDGE,{"derivedFrom":sQuery(id+"F39.wireOp",EDGE,"E27.bottom")}),1.0]])]});
            extrude(context, id + "F40", {"entities" : qUnion([Q0]), "operationType" : NewBodyOperationType.ADD, "depth" : 1.5 * mm});
        }
        {
            var Q0;
            Q0=makeQuery(id+"F1.opExtrude","SWEPT_FACE",FACE,{"disambiguationData":[OSD([sQuery(id+"F0.wireOp",EDGE,"E0.bottom")])]});
            var sketch = newSketch(context, id + "F41", { "sketchPlane" : qUnion([Q0])});
            skLineSegment(sketch, "E28.bottom", {"start": v(-15.67, -1.38) * mm, "end": v(-12.67, -1.37) * mm});
            skLineSegment(sketch, "E28.top", {"start": v(-15.67, -4.38) * mm, "end": v(-12.67, -4.38) * mm});
            skLineSegment(sketch, "E28.left", {"start": v(-15.67, -1.38) * mm, "end": v(-15.67, -4.38) * mm});
            skLineSegment(sketch, "E28.right", {"start": v(-12.67, -1.37) * mm, "end": v(-12.67, -4.37) * mm});
            skPoint(sketch, "E28.middle", {"position": v(-14.17, -2.88) * mm});
            skPoint(sketch, "E28.middle.positionSnap0", {"position": v(-14.17, -5.75) * mm});
            skPoint(sketch, "E28.middle.positionSnap1", {"position": v(-17.05, -2.88) * mm});
            skPoint(sketch, "E28.centerSnap0", {"position": v(-14.17, -5.75) * mm});
            skPoint(sketch, "E28.centerSnap1", {"position": v(-17.05, -2.88) * mm});
            skSolve(sketch);
        }
        {
            var Q0;
            Q0=makeQuery(id+"F41.imprint","IMPRINT",FACE,{"disambiguationData":[TD([[makeQuery(id+"F41.imprint","IMPRINT",EDGE,{"derivedFrom":sQuery(id+"F41.wireOp",EDGE,"E28.bottom")}),-1.0]])]});
            extrude(context, id + "F42", {"entities" : qUnion([Q0]), "operationType" : NewBodyOperationType.REMOVE, "oppositeDirection" : true, "depth" : 1.5 * mm});
        }
        {
            var Q0;
            Q0=makeQuery(id+"F1.opExtrude","SWEPT_FACE",FACE,{"disambiguationData":[OSD([sQuery(id+"F0.wireOp",EDGE,"E0.right")])]});
            var sketch = newSketch(context, id + "F43", { "sketchPlane" : qUnion([Q0])});
            skLineSegment(sketch, "E29.bottom", {"start": v(-4.38, 6.24) * mm, "end": v(-1.38, 6.24) * mm});
            skLineSegment(sketch, "E29.top", {"start": v(-4.37, 9.24) * mm, "end": v(-1.38, 9.24) * mm});
            skLineSegment(sketch, "E29.left", {"start": v(-4.38, 6.24) * mm, "end": v(-4.38, 9.24) * mm});
            skLineSegment(sketch, "E29.right", {"start": v(-1.38, 6.24) * mm, "end": v(-1.38, 9.24) * mm});
            skPoint(sketch, "E29.middle", {"position": v(-2.88, 7.74) * mm});
            skPoint(sketch, "E29.middle.positionSnap0", {"position": v(0, 7.74) * mm});
            skPoint(sketch, "E29.middle.positionSnap1", {"position": v(-2.88, 4.87) * mm});
            skPoint(sketch, "E29.centerSnap0", {"position": v(0, 7.74) * mm});
            skPoint(sketch, "E29.centerSnap1", {"position": v(-2.88, 4.87) * mm});
            skSolve(sketch);
        }
        {
            var Q0;
            Q0=makeQuery(id+"F43.imprint","IMPRINT",FACE,{"disambiguationData":[TD([[makeQuery(id+"F43.imprint","IMPRINT",EDGE,{"derivedFrom":sQuery(id+"F43.wireOp",EDGE,"E29.bottom")}),1.0]])]});
            extrude(context, id + "F44", {"entities" : qUnion([Q0]), "operationType" : NewBodyOperationType.REMOVE, "oppositeDirection" : true, "depth" : 1.5 * mm});
        }
        {
            var Q0;
            Q0=makeQuery(id+"F1.opExtrude","SWEPT_FACE",FACE,{"disambiguationData":[OSD([sQuery(id+"F0.wireOp",EDGE,"E2.right")])]});
            var sketch = newSketch(context, id + "F45", { "sketchPlane" : qUnion([Q0])});
            skLineSegment(sketch, "E30.bottom", {"start": v(-4.38, -9.83) * mm, "end": v(-1.38, -9.83) * mm});
            skLineSegment(sketch, "E30.top", {"start": v(-4.38, -6.83) * mm, "end": v(-1.38, -6.83) * mm});
            skLineSegment(sketch, "E30.left", {"start": v(-4.38, -9.83) * mm, "end": v(-4.38, -6.83) * mm});
            skLineSegment(sketch, "E30.right", {"start": v(-1.38, -9.83) * mm, "end": v(-1.38, -6.83) * mm});
            skPoint(sketch, "E30.middle", {"position": v(-2.88, -8.33) * mm});
            skPoint(sketch, "E30.middle.positionSnap0", {"position": v(0, -8.33) * mm});
            skPoint(sketch, "E30.middle.positionSnap1", {"position": v(-2.88, -11.2) * mm});
            skPoint(sketch, "E30.centerSnap0", {"position": v(0, -8.33) * mm});
            skPoint(sketch, "E30.centerSnap1", {"position": v(-2.88, -11.2) * mm});
            skSolve(sketch);
        }
        {
            var Q0;
            Q0 = qSketchRegion(id + "F45", true);
            extrude(context, id + "F46", {"entities" : qUnion([Q0]), "operationType" : NewBodyOperationType.REMOVE, "oppositeDirection" : true, "depth" : 1.5 * mm});
        }
        {
            var Q0;
            Q0=makeQuery(id+"F1.opExtrude","CAP_FACE",FACE,{"disambiguationData":[OSD([sQuery(id+"F0.wireOp",EDGE,"E2.bottom"),sQuery(id+"F0.wireOp",EDGE,"E2.top"),sQuery(id+"F0.wireOp",EDGE,"E2.left"),sQuery(id+"F0.wireOp",EDGE,"E2.right")])],"isStart":true});
            var sketch = newSketch(context, id + "F47", { "sketchPlane" : qUnion([Q0])});
            skLineSegment(sketch, "E31.bottom", {"start": v(-5.1, -6.83) * mm, "end": v(-8.1, -6.83) * mm});
            skLineSegment(sketch, "E31.top", {"start": v(-5.1, -9.83) * mm, "end": v(-8.1, -9.83) * mm});
            skLineSegment(sketch, "E31.left", {"start": v(-5.1, -6.83) * mm, "end": v(-5.1, -9.83) * mm});
            skLineSegment(sketch, "E31.right", {"start": v(-8.1, -6.83) * mm, "end": v(-8.1, -9.83) * mm});
            skPoint(sketch, "E31.middle", {"position": v(-6.6, -8.33) * mm});
            skPoint(sketch, "E31.middle.positionSnap0", {"position": v(-9.47, -8.33) * mm});
            skPoint(sketch, "E31.middle.positionSnap1", {"position": v(-6.6, -5.46) * mm});
            skPoint(sketch, "E31.centerSnap0", {"position": v(-9.47, -8.33) * mm});
            skPoint(sketch, "E31.centerSnap1", {"position": v(-6.6, -5.46) * mm});
            skSolve(sketch);
        }
        {
            var Q0;
            Q0 = qSketchRegion(id + "F47", true);
            var Q1;
            Q1=makeQuery(id+"F47.imprint","IMPRINT",FACE,{"disambiguationData":[TD([[makeQuery(id+"F47.imprint","IMPRINT",EDGE,{"derivedFrom":sQuery(id+"F47.wireOp",EDGE,"E31.bottom")}),1.0]])]});
            extrude(context, id + "F48", {"entities" : qUnion([Q0, Q1]), "operationType" : NewBodyOperationType.REMOVE, "oppositeDirection" : true, "depth" : 1.5 * mm});
        }
        {
            var Q0;
            Q0=makeQuery(id+"F1.opExtrude","SWEPT_FACE",FACE,{"disambiguationData":[OSD([sQuery(id+"F0.wireOp",EDGE,"E2.top")])]});
            var sketch = newSketch(context, id + "F49", { "sketchPlane" : qUnion([Q0])});
            skLineSegment(sketch, "E32.bottom", {"start": v(5.1, 1.38) * mm, "end": v(8.1, 1.38) * mm});
            skLineSegment(sketch, "E32.top", {"start": v(5.1, 4.38) * mm, "end": v(8.1, 4.38) * mm});
            skLineSegment(sketch, "E32.left", {"start": v(5.1, 1.38) * mm, "end": v(5.1, 4.38) * mm});
            skLineSegment(sketch, "E32.right", {"start": v(8.1, 1.38) * mm, "end": v(8.1, 4.38) * mm});
            skPoint(sketch, "E32.middle", {"position": v(6.6, 2.88) * mm});
            skPoint(sketch, "E32.middle.positionSnap0", {"position": v(9.47, 2.88) * mm});
            skPoint(sketch, "E32.middle.positionSnap1", {"position": v(6.6, 0) * mm});
            skPoint(sketch, "E32.centerSnap0", {"position": v(9.47, 2.88) * mm});
            skPoint(sketch, "E32.centerSnap1", {"position": v(6.6, 0) * mm});
            skSolve(sketch);
        }
        {
            var Q0;
            Q0=makeQuery(id+"F49.imprint","IMPRINT",FACE,{"disambiguationData":[TD([[makeQuery(id+"F49.imprint","IMPRINT",EDGE,{"derivedFrom":sQuery(id+"F49.wireOp",EDGE,"E32.bottom")}),1.0]])]});
            extrude(context, id + "F50", {"entities" : qUnion([Q0]), "operationType" : NewBodyOperationType.REMOVE, "oppositeDirection" : true, "depth" : 1.5 * mm});
        }
    });
